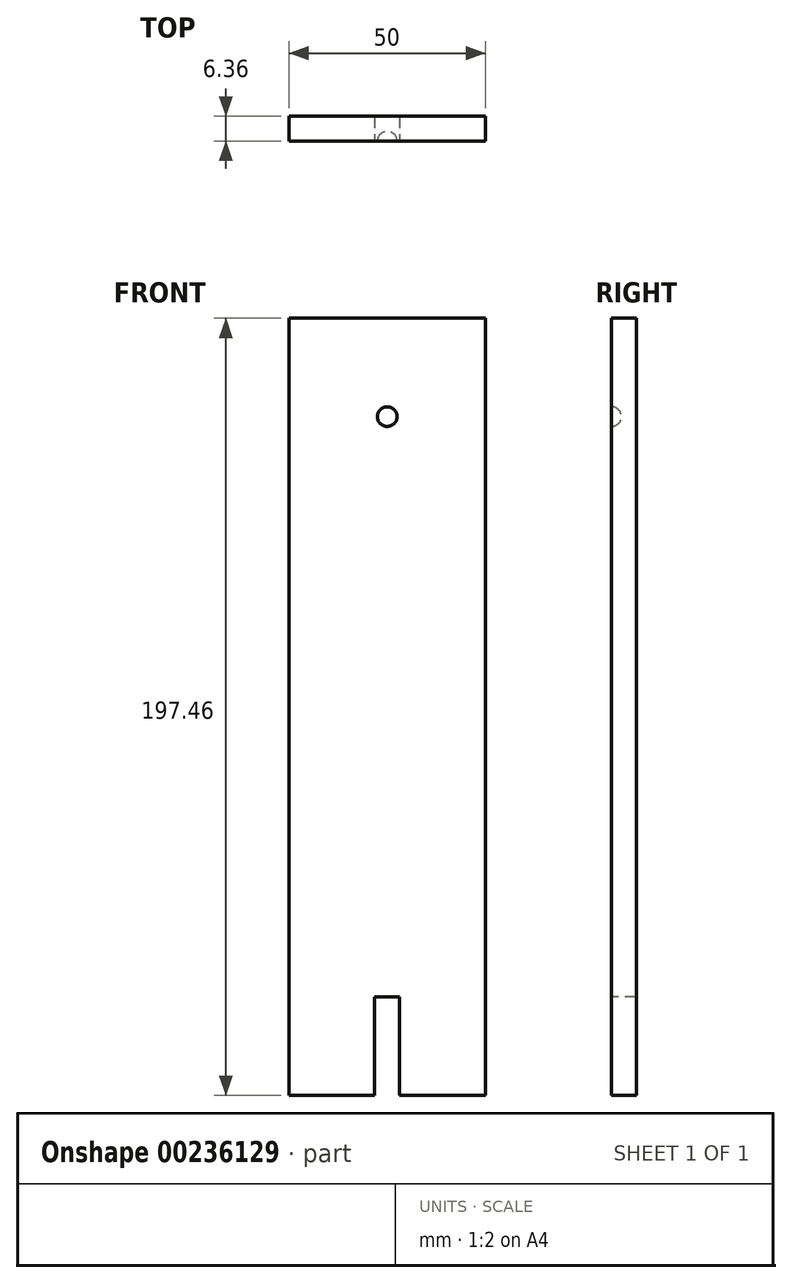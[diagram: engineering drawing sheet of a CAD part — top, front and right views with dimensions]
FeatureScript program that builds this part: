
annotation { "Feature Type Name" : "Feature", "Feature Type Description" : "" }
export const myFeature = defineFeature(function(context is Context, id is Id, definition is map)
    precondition{}
    {
        {
            var Q0;
            Q0=qCreatedBy(makeId("Front.planeOp"),FACE);
            var sketch = newSketch(context, id + "F0", { "sketchPlane" : qUnion([Q0])});
            skLineSegment(sketch, "E0.bottom", {"start": v(-25, 98.73) * mm, "end": v(25, 98.73) * mm});
            skLineSegment(sketch, "E0.top", {"start": v(-25, -98.73) * mm, "end": v(25, -98.73) * mm});
            skLineSegment(sketch, "E0.left", {"start": v(-25, 98.73) * mm, "end": v(-25, -98.73) * mm});
            skLineSegment(sketch, "E0.right", {"start": v(25, 98.73) * mm, "end": v(25, -98.73) * mm});
            skPoint(sketch, "E0.middle", {"position": v(0, 0) * mm});
            skSolve(sketch);
        }
        {
            var Q0;
            Q0 = qSketchRegion(id + "F0", true);
            extrude(context, id + "F1", {"entities" : qUnion([Q0]), "depth" : 6.35 * mm, "symmetric" : true});
        }
        {
            var Q0;
            Q0=makeQuery(id+"F1.opExtrude","CAP_FACE",FACE,{"disambiguationData":[OSD([sQuery(id+"F0.wireOp",EDGE,"E0.bottom"),sQuery(id+"F0.wireOp",EDGE,"E0.top"),sQuery(id+"F0.wireOp",EDGE,"E0.left"),sQuery(id+"F0.wireOp",EDGE,"E0.right")])],"isStart":false});
            var sketch = newSketch(context, id + "F2", { "sketchPlane" : qUnion([Q0])});
            skLineSegment(sketch, "E1", {"start": v(0, 76.23) * mm, "end": v(0, 71.23) * mm});
            skArc(sketch, "E2", {"start": v(0, 71.23) * mm, "mid": v(2.5, 73.73) * mm, "end": v(0, 76.23) * mm});
            skSolve(sketch);
        }
        {
            var Q0;
            Q0 = qSketchRegion(id + "F2", true);
            var Q1;
            Q1=sQuery(id+"F2.wireOp",EDGE,"E1");
            revolve(context, id + "F3", {"operationType" : NewBodyOperationType.REMOVE, "entities" : qUnion([Q0]), "axis" : qUnion([Q1]), "revolveType" : RevolveType.FULL, "oppositeDirection" : true});
        }
        {
            var Q0;
            Q0=makeQuery(id+"F1.opExtrude","CAP_FACE",FACE,{"disambiguationData":[OSD([sQuery(id+"F0.wireOp",EDGE,"E0.bottom"),sQuery(id+"F0.wireOp",EDGE,"E0.top"),sQuery(id+"F0.wireOp",EDGE,"E0.left"),sQuery(id+"F0.wireOp",EDGE,"E0.right")])],"isStart":false});
            var sketch = newSketch(context, id + "F4", { "sketchPlane" : qUnion([Q0])});
            skLineSegment(sketch, "E3.bottom", {"start": v(3.18, -98.73) * mm, "end": v(-3.17, -98.73) * mm});
            skLineSegment(sketch, "E3.top", {"start": v(3.17, -73.73) * mm, "end": v(-3.18, -73.73) * mm});
            skLineSegment(sketch, "E3.left", {"start": v(3.18, -98.73) * mm, "end": v(3.17, -73.73) * mm});
            skLineSegment(sketch, "E3.right", {"start": v(-3.17, -98.73) * mm, "end": v(-3.18, -73.73) * mm});
            skPoint(sketch, "E3.middle", {"position": v(0, -86.23) * mm});
            skSolve(sketch);
        }
        {
            var Q0;
            Q0 = qSketchRegion(id + "F4", true);
            extrude(context, id + "F5", {"entities" : qUnion([Q0]), "operationType" : NewBodyOperationType.REMOVE, "endBound" : BoundingType.THROUGH_ALL, "oppositeDirection" : true, "depth" : 25.4 * mm});
        }
    });
